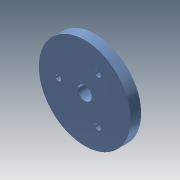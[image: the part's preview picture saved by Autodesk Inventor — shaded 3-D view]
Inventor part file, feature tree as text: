
AUTODESK INVENTOR PART (.ipt)
format: ipt  version: 2013 (Build 170138000, 138)  size: 107,008 bytes
history: native  units: mm
features: sketch x4, extrude x3
ambient origin geometry x8: Origin, YZ Plane, XZ Plane, XY Plane, X Axis, Y Axis, Z Axis, Center Point
bodies: Solid1 (feature_tree)
feature tree (7):
  extrude  "Extrusion1"  Depth=5.0mm
  extrude  "Extrusion2"  Depth=3.0mm
  extrude  "Extrusion3"  Depth=3.0mm
  sketch  "Sketch4"  dims[d9=3.8mm d10=0.0mm d11=2.0mm d12=2.0mm d13=2.0mm d14=3.8mm d15=0.0mm]
  sketch  "Sketch1"  dims[d0=33.15mm d1=5.0mm]
  sketch  "Sketch2"  dims[d2=3.8mm d3=0.0mm d4=3.0mm]
  sketch  "Sketch3"  dims[d7=3.0mm d8=3.0mm]
